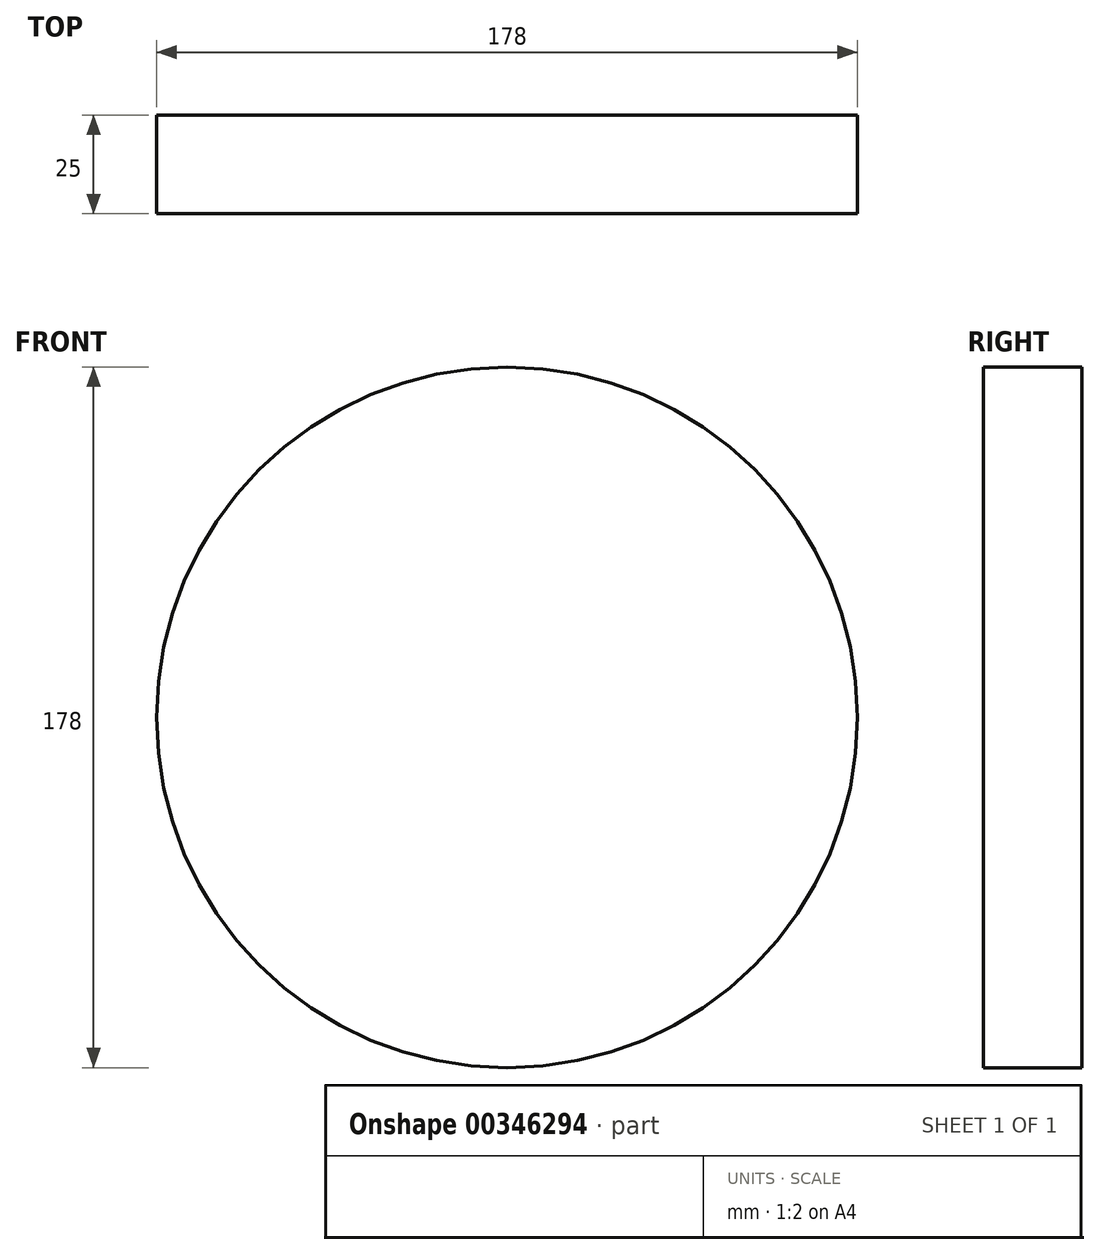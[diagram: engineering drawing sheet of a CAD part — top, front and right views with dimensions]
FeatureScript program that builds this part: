
annotation { "Feature Type Name" : "Feature", "Feature Type Description" : "" }
export const myFeature = defineFeature(function(context is Context, id is Id, definition is map)
    precondition{}
    {
        {
            var Q0;
            Q0=qCreatedBy(makeId("Front.planeOp"),FACE);
            var sketch = newSketch(context, id + "F0", { "sketchPlane" : qUnion([Q0])});
            skCircle(sketch, "E0", {"center": v(0, 0) * mm, "radius": 89 * mm});
            skSolve(sketch);
        }
        {
            var Q0;
            Q0 = qSketchRegion(id + "F0", true);
            extrude(context, id + "F1", {"entities" : qUnion([Q0]), "depth" : 25 * mm});
        }
    });
